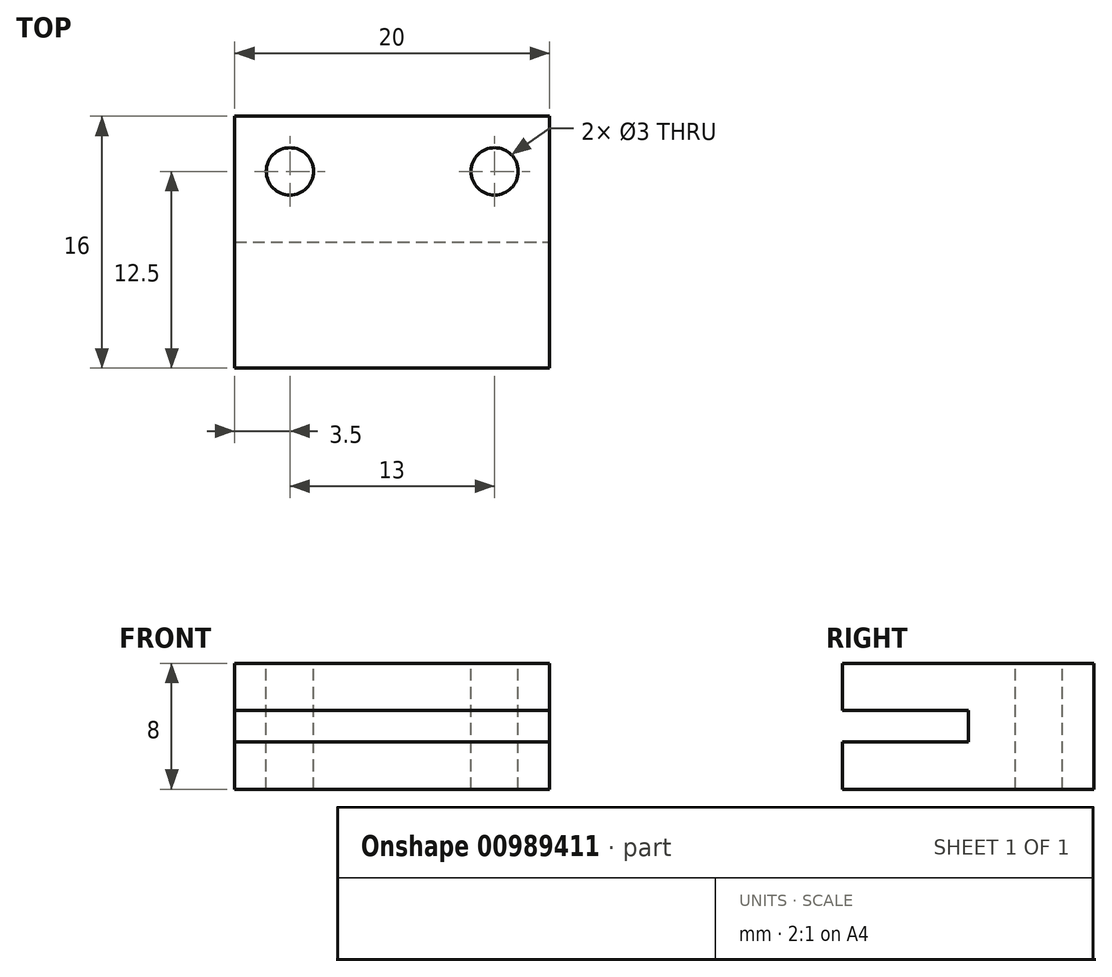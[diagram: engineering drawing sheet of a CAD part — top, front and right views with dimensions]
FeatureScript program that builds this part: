
annotation { "Feature Type Name" : "Feature", "Feature Type Description" : "" }
export const myFeature = defineFeature(function(context is Context, id is Id, definition is map)
    precondition{}
    {
        {
            var Q0;
            Q0=qCreatedBy(makeId("Front.planeOp"),FACE);
            var sketch = newSketch(context, id + "F0", { "sketchPlane" : qUnion([Q0])});
            skLineSegment(sketch, "E0.bottom", {"start": v(0, 0) * mm, "end": v(-20, 0) * mm});
            skLineSegment(sketch, "E0.top", {"start": v(0, 8) * mm, "end": v(-20, 8) * mm});
            skLineSegment(sketch, "E0.left", {"start": v(0, 0) * mm, "end": v(0, 8) * mm});
            skLineSegment(sketch, "E0.right", {"start": v(-20, 0) * mm, "end": v(-20, 8) * mm});
            skSolve(sketch);
        }
        {
            var Q0;
            Q0=makeQuery(id+"F0.imprint","IMPRINT",FACE,{"disambiguationData":[TD([[makeQuery(id+"F0.imprint","IMPRINT",EDGE,{"derivedFrom":sQuery(id+"F0.wireOp",EDGE,"E0.bottom")}),-1.0]])]});
            extrude(context, id + "F1", {"entities" : qUnion([Q0]), "depth" : 16 * mm, "offsetDistance" : 25 * mm});
        }
        {
            var Q0;
            Q0=makeQuery(id+"F1.opExtrude","CAP_FACE",FACE,{"disambiguationData":[OSD([sQuery(id+"F0.wireOp",EDGE,"E0.bottom"),sQuery(id+"F0.wireOp",EDGE,"E0.top"),sQuery(id+"F0.wireOp",EDGE,"E0.left"),sQuery(id+"F0.wireOp",EDGE,"E0.right")])],"isStart":false});
            var sketch = newSketch(context, id + "F2", { "sketchPlane" : qUnion([Q0])});
            skLineSegment(sketch, "E1.bottom", {"start": v(-20, 5) * mm, "end": v(0, 5) * mm});
            skLineSegment(sketch, "E1.top", {"start": v(-20, 3) * mm, "end": v(0, 3) * mm});
            skLineSegment(sketch, "E1.left", {"start": v(-20, 5) * mm, "end": v(-20, 3) * mm});
            skLineSegment(sketch, "E1.right", {"start": v(0, 5) * mm, "end": v(0, 3) * mm});
            skSolve(sketch);
        }
        {
            var Q0;
            Q0=makeQuery(id+"F2.imprint","IMPRINT",FACE,{"disambiguationData":[TD([[makeQuery(id+"F2.imprint","IMPRINT",EDGE,{"derivedFrom":sQuery(id+"F2.wireOp",EDGE,"E1.bottom")}),-1.0]])]});
            extrude(context, id + "F3", {"entities" : qUnion([Q0]), "operationType" : NewBodyOperationType.REMOVE, "oppositeDirection" : true, "depth" : 8 * mm, "offsetDistance" : 25 * mm});
        }
        {
            var Q0;
            Q0=makeQuery(id+"F1.opExtrude","SWEPT_FACE",FACE,{"disambiguationData":[OSD([sQuery(id+"F0.wireOp",EDGE,"E0.top")])]});
            var sketch = newSketch(context, id + "F4", { "sketchPlane" : qUnion([Q0])});
            skCircle(sketch, "E2", {"center": v(-16.5, -3.5) * mm, "radius": 1.5 * mm});
            skCircle(sketch, "E3", {"center": v(-3.5, -3.5) * mm, "radius": 1.5 * mm});
            skSolve(sketch);
        }
        {
            var Q0;
            Q0 = qSketchRegion(id + "F4", true);
            var Q1;
            Q1=makeQuery(id+"F4.imprint","IMPRINT",FACE,{"disambiguationData":[TD([[makeQuery(id+"F4.imprint","IMPRINT",EDGE,{"derivedFrom":sQuery(id+"F4.wireOp",EDGE,"E2")}),1.0]])]});
            extrude(context, id + "F5", {"entities" : qUnion([Q0, Q1]), "operationType" : NewBodyOperationType.REMOVE, "oppositeDirection" : true, "depth" : 25 * mm, "offsetDistance" : 25 * mm});
        }
    });
